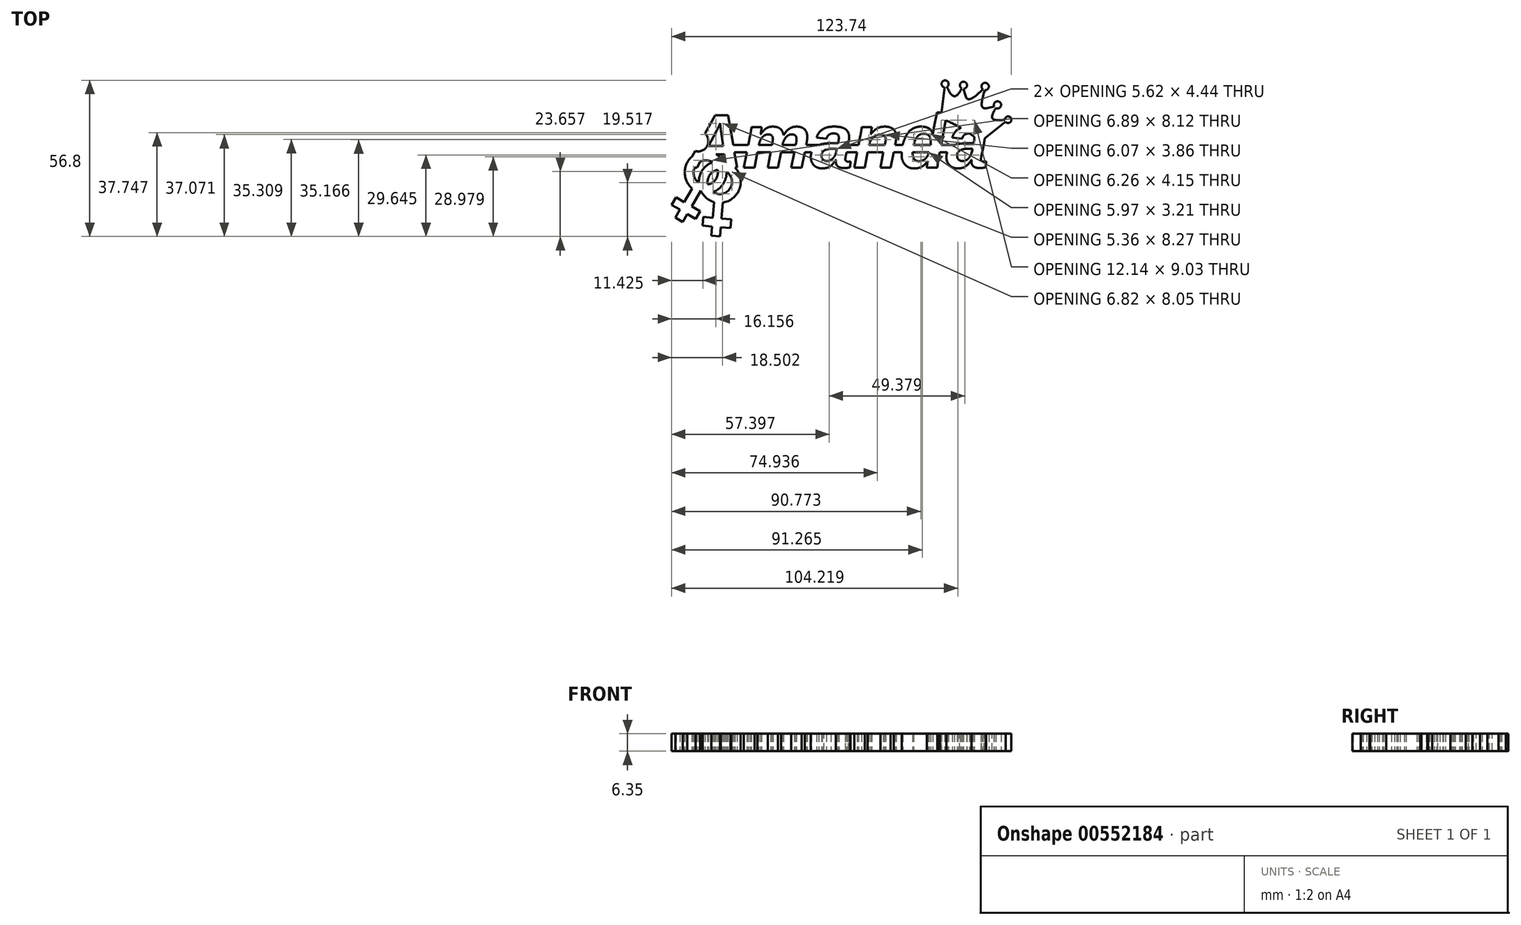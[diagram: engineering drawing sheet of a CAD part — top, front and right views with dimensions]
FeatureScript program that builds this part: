
annotation { "Feature Type Name" : "Feature", "Feature Type Description" : "" }
export const myFeature = defineFeature(function(context is Context, id is Id, definition is map)
    precondition{}
    {
        {
            var Q0;
            Q0=qCreatedBy(makeId("Top.planeOp"),FACE);
            var sketch = newSketch(context, id + "F0", { "sketchPlane" : qUnion([Q0])});
            skText(sketch, "E0", { "text": "Amanda", "fontName": "Arimo-BoldItalic.ttf"});
            skLineSegment(sketch, "E1.bottom", {"start": v(-56.87, 8.2) * mm, "end": v(37.6, 8.2) * mm});
            skLineSegment(sketch, "E1.top", {"start": v(-56.87, 5.54) * mm, "end": v(37.6, 5.54) * mm});
            skLineSegment(sketch, "E1.left", {"start": v(-56.87, 8.2) * mm, "end": v(-56.87, 5.54) * mm});
            skLineSegment(sketch, "E1.right", {"start": v(37.6, 8.2) * mm, "end": v(37.6, 5.54) * mm});
            skCircle(sketch, "E2", {"center": v(-65.8, 9.64) * mm, "radius": 3.75 * mm});
            const initialGuessF0  = {"E0": [-0.06965, 0, 1, 0, 0.02]};
            skSetInitialGuess(sketch, initialGuessF0);
            skSolve(sketch);
        }
        {
            var Q0;
            {var subQ0=sQuery(id+"F0.wireOp",EDGE,"E2");var subQ1=sQuery(id+"F0.wireOp",EDGE,"E0.sketch_text.stroke-4");var subQ2=makeQuery(id+"F0.imprint","INTERSECT",VERTEX,{"disambiguationData":[OD(0.0)],"derivedFrom":[subQ1,subQ0]});Q0=makeQuery(id+"F0.imprint","IMPRINT",FACE,{"disambiguationData":[TD([[makeQuery(id+"F0.imprint","IMPRINT",EDGE,{"disambiguationData":[TD([[subQ2,-1.0]])],"derivedFrom":subQ1}),1.0]])]});}
            var Q1;
            {var subQ0=sQuery(id+"F0.wireOp",EDGE,"E0.sketch_text.stroke-16");Q1=makeQuery(id+"F0.imprint","IMPRINT",FACE,{"disambiguationData":[TD([[makeQuery(id+"F0.imprint","IMPRINT",EDGE,{"derivedFrom":subQ0}),-1.0]])]});}
            var Q2;
            {var subQ0=sQuery(id+"F0.wireOp",EDGE,"E0.sketch_text.stroke-23");Q2=makeQuery(id+"F0.imprint","IMPRINT",FACE,{"disambiguationData":[TD([[makeQuery(id+"F0.imprint","IMPRINT",EDGE,{"derivedFrom":subQ0}),-1.0]])]});}
            var Q3;
            {var subQ0=sQuery(id+"F0.wireOp",EDGE,"E0.sketch_text.stroke-40");Q3=makeQuery(id+"F0.imprint","IMPRINT",FACE,{"disambiguationData":[TD([[makeQuery(id+"F0.imprint","IMPRINT",EDGE,{"derivedFrom":subQ0}),-1.0]])]});}
            var Q4;
            {var subQ0=sQuery(id+"F0.wireOp",EDGE,"E0.sketch_text.stroke-55");Q4=makeQuery(id+"F0.imprint","IMPRINT",FACE,{"disambiguationData":[TD([[makeQuery(id+"F0.imprint","IMPRINT",EDGE,{"derivedFrom":subQ0}),-1.0]])]});}
            var Q5;
            {var subQ0=sQuery(id+"F0.wireOp",EDGE,"E0.sketch_text.stroke-104");Q5=makeQuery(id+"F0.imprint","IMPRINT",FACE,{"disambiguationData":[TD([[makeQuery(id+"F0.imprint","IMPRINT",EDGE,{"derivedFrom":subQ0}),-1.0]])]});}
            var Q6;
            {var subQ0=sQuery(id+"F0.wireOp",EDGE,"E0.sketch_text.stroke-90");Q6=makeQuery(id+"F0.imprint","IMPRINT",FACE,{"disambiguationData":[TD([[makeQuery(id+"F0.imprint","IMPRINT",EDGE,{"derivedFrom":subQ0}),-1.0]])]});}
            var Q7;
            {var subQ0=sQuery(id+"F0.wireOp",EDGE,"E2");var subQ1=sQuery(id+"F0.wireOp",EDGE,"E0.sketch_text.stroke-4");var subQ2=makeQuery(id+"F0.imprint","INTERSECT",VERTEX,{"disambiguationData":[OD(0.0)],"derivedFrom":[subQ1,subQ0]});Q7=makeQuery(id+"F0.imprint","IMPRINT",FACE,{"disambiguationData":[TD([[makeQuery(id+"F0.imprint","IMPRINT",EDGE,{"disambiguationData":[TD([[subQ2,-1.0]])],"derivedFrom":subQ1}),-1.0]])]});}
            var Q8;
            {var subQ0=sQuery(id+"F0.wireOp",EDGE,"E1.bottom");var subQ1=sQuery(id+"F0.wireOp",EDGE,"E0.sketch_text.stroke-6");var subQ2=makeQuery(id+"F0.imprint","INTERSECT",VERTEX,{"derivedFrom":[subQ1,subQ0]});Q8=makeQuery(id+"F0.imprint","IMPRINT",FACE,{"disambiguationData":[TD([[makeQuery(id+"F0.imprint","IMPRINT",EDGE,{"disambiguationData":[TD([[subQ2,-1.0]])],"derivedFrom":subQ1}),1.0]])]});}
            var Q9;
            {var subQ3=sQuery(id+"F0.wireOp",EDGE,"E1.bottom");var subQ7=sQuery(id+"F0.wireOp",EDGE,"E0.sketch_text.stroke-39");var subQ8=makeQuery(id+"F0.imprint","INTERSECT",VERTEX,{"derivedFrom":[subQ7,subQ3]});Q9=makeQuery(id+"F0.imprint","IMPRINT",FACE,{"disambiguationData":[TD([[makeQuery(id+"F0.imprint","IMPRINT",EDGE,{"disambiguationData":[TD([[subQ8,-1.0]])],"derivedFrom":subQ7}),1.0]])]});}
            var Q10;
            Q10=makeQuery(id+"F0.imprint","IMPRINT",FACE,{"disambiguationData":[TD([[makeQuery(id+"F0.imprint","IMPRINT",EDGE,{"derivedFrom":sQuery(id+"F0.wireOp",EDGE,"E0.sketch_text.stroke-45")}),-1.0]])]});
            var Q11;
            {var subQ0=sQuery(id+"F0.wireOp",EDGE,"E1.bottom");var subQ1=sQuery(id+"F0.wireOp",EDGE,"E0.sketch_text.stroke-103");var subQ2=makeQuery(id+"F0.imprint","INTERSECT",VERTEX,{"derivedFrom":[subQ1,subQ0]});Q11=makeQuery(id+"F0.imprint","IMPRINT",FACE,{"disambiguationData":[TD([[makeQuery(id+"F0.imprint","IMPRINT",EDGE,{"disambiguationData":[TD([[subQ2,-1.0]])],"derivedFrom":subQ1}),1.0]])]});}
            var Q12;
            {var subQ0=sQuery(id+"F0.wireOp",EDGE,"E1.bottom");var subQ1=sQuery(id+"F0.wireOp",EDGE,"E0.sketch_text.stroke-118");var subQ2=makeQuery(id+"F0.imprint","INTERSECT",VERTEX,{"derivedFrom":[subQ1,subQ0]});Q12=makeQuery(id+"F0.imprint","IMPRINT",FACE,{"disambiguationData":[TD([[makeQuery(id+"F0.imprint","IMPRINT",EDGE,{"disambiguationData":[TD([[subQ2,-1.0]])],"derivedFrom":subQ1}),1.0]])]});}
            var Q13;
            Q13=makeQuery(id+"F0.imprint","IMPRINT",FACE,{"disambiguationData":[TD([[makeQuery(id+"F0.imprint","IMPRINT",EDGE,{"derivedFrom":sQuery(id+"F0.wireOp",EDGE,"E0.sketch_text.stroke-133")}),-1.0]])]});
            var Q14;
            Q14=makeQuery(id+"F0.imprint","IMPRINT",FACE,{"disambiguationData":[TD([[makeQuery(id+"F0.imprint","IMPRINT",EDGE,{"derivedFrom":sQuery(id+"F0.wireOp",EDGE,"E0.sketch_text.stroke-0")}),-1.0]])]});
            var Q15;
            {var subQ0=sQuery(id+"F0.wireOp",EDGE,"E1.bottom");var subQ1=sQuery(id+"F0.wireOp",EDGE,"E0.sketch_text.stroke-6");var subQ2=makeQuery(id+"F0.imprint","INTERSECT",VERTEX,{"derivedFrom":[subQ1,subQ0]});Q15=makeQuery(id+"F0.imprint","IMPRINT",FACE,{"disambiguationData":[TD([[makeQuery(id+"F0.imprint","IMPRINT",EDGE,{"disambiguationData":[TD([[subQ2,-1.0]])],"derivedFrom":subQ1}),-1.0]])]});}
            var Q16;
            {var subQ1=sQuery(id+"F0.wireOp",EDGE,"E0.sketch_text.stroke-85");var subQ7=sQuery(id+"F0.wireOp",EDGE,"E0.sketch_text.stroke-84");var subQ8=makeQuery(id+"F0.imprint","INTERSECT",VERTEX,{"derivedFrom":[subQ7,subQ1]});Q16=makeQuery(id+"F0.imprint","IMPRINT",FACE,{"disambiguationData":[TD([[makeQuery(id+"F0.imprint","IMPRINT",EDGE,{"disambiguationData":[TD([[subQ8,1.0]])],"derivedFrom":subQ7}),1.0]])]});}
            var Q17;
            {var subQ7=sQuery(id+"F0.wireOp",EDGE,"E0.sketch_text.stroke-86");Q17=makeQuery(id+"F0.imprint","IMPRINT",FACE,{"disambiguationData":[TD([[makeQuery(id+"F0.imprint","IMPRINT",EDGE,{"derivedFrom":subQ7}),-1.0]])]});}
            var Q18;
            Q18=makeQuery(id+"F0.imprint","IMPRINT",FACE,{"disambiguationData":[TD([[makeQuery(id+"F0.imprint","IMPRINT",EDGE,{"derivedFrom":sQuery(id+"F0.wireOp",EDGE,"E0.sketch_text.stroke-105")}),-1.0]])]});
            var Q19;
            {var subQ4=sQuery(id+"F0.wireOp",EDGE,"E0.sketch_text.stroke-110");Q19=makeQuery(id+"F0.imprint","IMPRINT",FACE,{"disambiguationData":[TD([[makeQuery(id+"F0.imprint","IMPRINT",EDGE,{"derivedFrom":subQ4}),-1.0]])]});}
            var Q20;
            Q20=makeQuery(id+"F0.imprint","IMPRINT",FACE,{"disambiguationData":[TD([[makeQuery(id+"F0.imprint","IMPRINT",EDGE,{"derivedFrom":sQuery(id+"F0.wireOp",EDGE,"E0.sketch_text.stroke-164")}),-1.0]])]});
            var Q21;
            {var subQ0=sQuery(id+"F0.wireOp",EDGE,"E1.top");var subQ1=sQuery(id+"F0.wireOp",EDGE,"E0.sketch_text.stroke-15");var subQ2=makeQuery(id+"F0.imprint","INTERSECT",VERTEX,{"derivedFrom":[subQ1,subQ0]});Q21=makeQuery(id+"F0.imprint","IMPRINT",FACE,{"disambiguationData":[TD([[makeQuery(id+"F0.imprint","IMPRINT",EDGE,{"disambiguationData":[TD([[subQ2,1.0]])],"derivedFrom":subQ1}),-1.0]])]});}
            var Q22;
            {var subQ0=sQuery(id+"F0.wireOp",EDGE,"E1.top");var subQ1=sQuery(id+"F0.wireOp",EDGE,"E0.sketch_text.stroke-22");var subQ2=makeQuery(id+"F0.imprint","INTERSECT",VERTEX,{"derivedFrom":[subQ1,subQ0]});Q22=makeQuery(id+"F0.imprint","IMPRINT",FACE,{"disambiguationData":[TD([[makeQuery(id+"F0.imprint","IMPRINT",EDGE,{"disambiguationData":[TD([[subQ2,1.0]])],"derivedFrom":subQ1}),-1.0]])]});}
            var Q23;
            {var subQ0=sQuery(id+"F0.wireOp",EDGE,"E1.bottom");var subQ1=sQuery(id+"F0.wireOp",EDGE,"E0.sketch_text.stroke-39");var subQ2=makeQuery(id+"F0.imprint","INTERSECT",VERTEX,{"derivedFrom":[subQ1,subQ0]});Q23=makeQuery(id+"F0.imprint","IMPRINT",FACE,{"disambiguationData":[TD([[makeQuery(id+"F0.imprint","IMPRINT",EDGE,{"disambiguationData":[TD([[subQ2,-1.0]])],"derivedFrom":subQ1}),-1.0]])]});}
            var Q24;
            {var subQ0=sQuery(id+"F0.wireOp",EDGE,"E0.sketch_text.stroke-85");var subQ1=sQuery(id+"F0.wireOp",EDGE,"E0.sketch_text.stroke-84");var subQ2=makeQuery(id+"F0.imprint","INTERSECT",VERTEX,{"derivedFrom":[subQ1,subQ0]});Q24=makeQuery(id+"F0.imprint","IMPRINT",FACE,{"disambiguationData":[TD([[makeQuery(id+"F0.imprint","IMPRINT",EDGE,{"disambiguationData":[TD([[subQ2,1.0]])],"derivedFrom":subQ1}),-1.0]])]});}
            var Q25;
            {var subQ0=sQuery(id+"F0.wireOp",EDGE,"E1.top");var subQ1=sQuery(id+"F0.wireOp",EDGE,"E0.sketch_text.stroke-89");var subQ2=makeQuery(id+"F0.imprint","INTERSECT",VERTEX,{"derivedFrom":[subQ1,subQ0]});Q25=makeQuery(id+"F0.imprint","IMPRINT",FACE,{"disambiguationData":[TD([[makeQuery(id+"F0.imprint","IMPRINT",EDGE,{"disambiguationData":[TD([[subQ2,1.0]])],"derivedFrom":subQ1}),-1.0]])]});}
            var Q26;
            {var subQ0=sQuery(id+"F0.wireOp",EDGE,"E1.top");var subQ1=sQuery(id+"F0.wireOp",EDGE,"E0.sketch_text.stroke-109");var subQ2=makeQuery(id+"F0.imprint","INTERSECT",VERTEX,{"derivedFrom":[subQ1,subQ0]});Q26=makeQuery(id+"F0.imprint","IMPRINT",FACE,{"disambiguationData":[TD([[makeQuery(id+"F0.imprint","IMPRINT",EDGE,{"disambiguationData":[TD([[subQ2,-1.0]])],"derivedFrom":subQ1}),-1.0]])]});}
            var Q27;
            {var subQ5=sQuery(id+"F0.wireOp",EDGE,"E1.bottom");var subQ6=sQuery(id+"F0.wireOp",EDGE,"E0.sketch_text.stroke-118");var subQ7=makeQuery(id+"F0.imprint","INTERSECT",VERTEX,{"derivedFrom":[subQ6,subQ5]});Q27=makeQuery(id+"F0.imprint","IMPRINT",FACE,{"disambiguationData":[TD([[makeQuery(id+"F0.imprint","IMPRINT",EDGE,{"disambiguationData":[TD([[subQ7,-1.0]])],"derivedFrom":subQ6}),-1.0]])]});}
            var Q28;
            Q28=makeQuery(id+"F0.imprint","IMPRINT",FACE,{"disambiguationData":[TD([[makeQuery(id+"F0.imprint","IMPRINT",EDGE,{"derivedFrom":sQuery(id+"F0.wireOp",EDGE,"E0.sketch_text.stroke-13")}),-1.0]])]});
            var Q29;
            Q29=makeQuery(id+"F0.imprint","IMPRINT",FACE,{"disambiguationData":[TD([[makeQuery(id+"F0.imprint","IMPRINT",EDGE,{"derivedFrom":sQuery(id+"F0.wireOp",EDGE,"E0.sketch_text.stroke-76")}),-1.0]])]});
            var Q30;
            {var subQ0=sQuery(id+"F0.wireOp",EDGE,"E1.bottom");var subQ1=sQuery(id+"F0.wireOp",EDGE,"E0.sketch_text.stroke-66");var subQ2=makeQuery(id+"F0.imprint","INTERSECT",VERTEX,{"derivedFrom":[subQ1,subQ0]});Q30=makeQuery(id+"F0.imprint","IMPRINT",FACE,{"disambiguationData":[TD([[makeQuery(id+"F0.imprint","IMPRINT",EDGE,{"disambiguationData":[TD([[subQ2,-1.0]])],"derivedFrom":subQ1}),1.0]])]});}
            var Q31;
            {var subQ0=sQuery(id+"F0.wireOp",EDGE,"E1.top");var subQ1=sQuery(id+"F0.wireOp",EDGE,"E0.sketch_text.stroke-17");var subQ2=makeQuery(id+"F0.imprint","INTERSECT",VERTEX,{"derivedFrom":[subQ1,subQ0]});Q31=makeQuery(id+"F0.imprint","IMPRINT",FACE,{"disambiguationData":[TD([[makeQuery(id+"F0.imprint","IMPRINT",EDGE,{"disambiguationData":[TD([[subQ2,-1.0]])],"derivedFrom":subQ1}),1.0]])]});}
            var Q32;
            {var subQ0=sQuery(id+"F0.wireOp",EDGE,"E1.top");var subQ1=sQuery(id+"F0.wireOp",EDGE,"E0.sketch_text.stroke-15");var subQ2=makeQuery(id+"F0.imprint","INTERSECT",VERTEX,{"derivedFrom":[subQ1,subQ0]});Q32=makeQuery(id+"F0.imprint","IMPRINT",FACE,{"disambiguationData":[TD([[makeQuery(id+"F0.imprint","IMPRINT",EDGE,{"disambiguationData":[TD([[subQ2,1.0]])],"derivedFrom":subQ1}),1.0]])]});}
            var Q33;
            {var subQ5=sQuery(id+"F0.wireOp",EDGE,"E0.sketch_text.stroke-126");var subQ6=sQuery(id+"F0.wireOp",EDGE,"E0.sketch_text.stroke-125");var subQ7=makeQuery(id+"F0.imprint","INTERSECT",VERTEX,{"derivedFrom":[subQ6,subQ5]});Q33=makeQuery(id+"F0.imprint","IMPRINT",FACE,{"disambiguationData":[TD([[makeQuery(id+"F0.imprint","IMPRINT",EDGE,{"disambiguationData":[TD([[subQ7,1.0]])],"derivedFrom":subQ6}),1.0]])]});}
            extrude(context, id + "F1", {"entities" : qUnion([Q0, Q1, Q2, Q3, Q4, Q5, Q6, Q7, Q8, Q9, Q10, Q11, Q12, Q13, Q14, Q15, Q16, Q17, Q18, Q19, Q20, Q21, Q22, Q23, Q24, Q25, Q26, Q27, Q28, Q29, Q30, Q31, Q32, Q33]), "depth" : 6.35 * mm, "offsetDistance" : 25.4 * mm});
        }
        {
            var Q0;
            Q0=qCreatedBy(makeId("Top.planeOp"),FACE);
            var sketch = newSketch(context, id + "F2", { "sketchPlane" : qUnion([Q0])});
            skCircle(sketch, "E3", {"center": v(24.15, 30.47) * mm, "radius": 1.29 * mm});
            skCircle(sketch, "E4", {"center": v(30.85, 29.98) * mm, "radius": 1.29 * mm});
            skCircle(sketch, "E5", {"center": v(38.74, 29.54) * mm, "radius": 1.34 * mm});
            skCircle(sketch, "E6", {"center": v(43.23, 22.83) * mm, "radius": 1.31 * mm});
            skCircle(sketch, "E7", {"center": v(47.1, 17.44) * mm, "radius": 1.2 * mm});
            skArc(sketch, "E8", {"start": v(36.96, 9.42) * mm, "mid": v(30.12, 14.34) * mm, "end": v(22.52, 17.98) * mm});
            skLineSegment(sketch, "E9", {"start": v(22.52, 17.98) * mm, "end": v(24.01, 29.19) * mm});
            skLineSegment(sketch, "E10", {"start": v(36.96, 9.42) * mm, "end": v(46.15, 16.72) * mm});
            skFitSpline(sketch, "E11", {"points": [v(24.83, 29.38) * mm, v(26.19, 26.87) * mm, v(27.5, 25.97) * mm, v(28.7, 26.52) * mm, v(30.2, 28.87) * mm], "startDerivative": vector(4.21, -9.4) * mm, "endDerivative": vector(4.9, 9.23) * mm});
            skFitSpline(sketch, "E12", {"points": [v(30.88, 28.7) * mm, v(31.53, 26.21) * mm, v(32.42, 24.96) * mm, v(34.21, 25.4) * mm, v(37.92, 28.47) * mm], "startDerivative": vector(2.23, -10.4) * mm, "endDerivative": vector(11.24, 10.52) * mm});
            skFitSpline(sketch, "E13", {"points": [v(38.61, 28.2) * mm, v(37.45, 23.38) * mm, v(37.98, 21.75) * mm, v(42.03, 22.3) * mm], "startDerivative": vector(-4, -13.13) * mm, "endDerivative": vector(13.55, 3.8) * mm});
            skFitSpline(sketch, "E14", {"points": [v(42.65, 21.66) * mm, v(41.4, 19.27) * mm, v(41.64, 17.66) * mm, v(45.9, 17.39) * mm], "startDerivative": vector(-4.66, -7.18) * mm, "endDerivative": vector(12.9, 1.1) * mm});
            skSolve(sketch);
        }
        {
            var Q0;
            Q0=makeQuery(id+"F2.imprint","IMPRINT",FACE,{"disambiguationData":[TD([[makeQuery(id+"F2.imprint","IMPRINT",EDGE,{"derivedFrom":sQuery(id+"F2.wireOp",EDGE,"E8")}),-1.0]])]});
            var Q1;
            {var subQ0=sQuery(id+"F2.wireOp",EDGE,"E5");var subQ1=makeQuery(id+"F2.imprint","INTERSECT",VERTEX,{"derivedFrom":[subQ0,sQuery(id+"F2.wireOp",EDGE,"E12")]});Q1=makeQuery(id+"F2.imprint","IMPRINT",FACE,{"disambiguationData":[TD([[makeQuery(id+"F2.imprint","IMPRINT",EDGE,{"disambiguationData":[TD([[subQ1,-1.0]])],"derivedFrom":subQ0}),1.0]])]});}
            var Q2;
            {var subQ0=sQuery(id+"F2.wireOp",EDGE,"E4");var subQ1=makeQuery(id+"F2.imprint","INTERSECT",VERTEX,{"derivedFrom":[subQ0,sQuery(id+"F2.wireOp",EDGE,"E11")]});Q2=makeQuery(id+"F2.imprint","IMPRINT",FACE,{"disambiguationData":[TD([[makeQuery(id+"F2.imprint","IMPRINT",EDGE,{"disambiguationData":[TD([[subQ1,-1.0]])],"derivedFrom":subQ0}),1.0]])]});}
            var Q3;
            {var subQ0=sQuery(id+"F2.wireOp",EDGE,"E3");var subQ1=makeQuery(id+"F2.imprint","INTERSECT",VERTEX,{"derivedFrom":[subQ0,sQuery(id+"F2.wireOp",EDGE,"E9")]});Q3=makeQuery(id+"F2.imprint","IMPRINT",FACE,{"disambiguationData":[TD([[makeQuery(id+"F2.imprint","IMPRINT",EDGE,{"disambiguationData":[TD([[subQ1,-1.0]])],"derivedFrom":subQ0}),1.0]])]});}
            var Q4;
            {var subQ0=sQuery(id+"F2.wireOp",EDGE,"E6");var subQ1=makeQuery(id+"F2.imprint","INTERSECT",VERTEX,{"derivedFrom":[subQ0,sQuery(id+"F2.wireOp",EDGE,"E13")]});Q4=makeQuery(id+"F2.imprint","IMPRINT",FACE,{"disambiguationData":[TD([[makeQuery(id+"F2.imprint","IMPRINT",EDGE,{"disambiguationData":[TD([[subQ1,-1.0]])],"derivedFrom":subQ0}),1.0]])]});}
            var Q5;
            {var subQ0=sQuery(id+"F2.wireOp",EDGE,"E7");var subQ1=makeQuery(id+"F2.imprint","INTERSECT",VERTEX,{"derivedFrom":[subQ0,sQuery(id+"F2.wireOp",EDGE,"E10")]});Q5=makeQuery(id+"F2.imprint","IMPRINT",FACE,{"disambiguationData":[TD([[makeQuery(id+"F2.imprint","IMPRINT",EDGE,{"disambiguationData":[TD([[subQ1,1.0]])],"derivedFrom":subQ0}),1.0]])]});}
            extrude(context, id + "F3", {"entities" : qUnion([Q0, Q1, Q2, Q3, Q4, Q5]), "operationType" : NewBodyOperationType.ADD, "depth" : 6.35 * mm, "offsetDistance" : 25.4 * mm});
        }
        {
            var Q0;
            Q0=qCreatedBy(makeId("Top.planeOp"),FACE);
            var sketch = newSketch(context, id + "F4", { "sketchPlane" : qUnion([Q0])});
            skCircle(sketch, "E15", {"center": v(-63.03, -1.76) * mm, "radius": 4.45 * mm});
            skCircle(sketch, "E16", {"center": v(-63.03, -1.76) * mm, "radius": 7.62 * mm});
            skLineSegment(sketch, "E17.bottom", {"start": v(-66.5, -5) * mm, "end": v(-63.75, -6.58) * mm});
            skLineSegment(sketch, "E17.top", {"start": v(-74.12, -18.19) * mm, "end": v(-71.37, -19.78) * mm});
            skLineSegment(sketch, "E17.left", {"start": v(-66.5, -5) * mm, "end": v(-74.12, -18.19) * mm});
            skLineSegment(sketch, "E17.right", {"start": v(-63.75, -6.58) * mm, "end": v(-71.37, -19.78) * mm});
            skLineSegment(sketch, "E18.bottom", {"start": v(-73.86, -10.79) * mm, "end": v(-65.06, -15.87) * mm});
            skLineSegment(sketch, "E18.top", {"start": v(-75.45, -13.53) * mm, "end": v(-66.65, -18.61) * mm});
            skLineSegment(sketch, "E18.left", {"start": v(-73.86, -10.79) * mm, "end": v(-75.45, -13.53) * mm});
            skLineSegment(sketch, "E18.right", {"start": v(-65.06, -15.87) * mm, "end": v(-66.65, -18.61) * mm});
            skLineSegment(sketch, "E19.1.0.0", {"start": v(-61, -24.76) * mm, "end": v(-57.84, -25.04) * mm});
            skLineSegment(sketch, "E19.1.0.1", {"start": v(-59.67, -9.58) * mm, "end": v(-61, -24.76) * mm});
            skLineSegment(sketch, "E19.1.0.2", {"start": v(-56.51, -9.86) * mm, "end": v(-57.84, -25.04) * mm});
            skLineSegment(sketch, "E19.1.0.3", {"start": v(-63.9, -17.94) * mm, "end": v(-53.78, -18.83) * mm});
            skCircle(sketch, "E19.1.0.4", {"center": v(-57.9, -5.19) * mm, "radius": 7.62 * mm});
            skLineSegment(sketch, "E19.1.0.5", {"start": v(-59.67, -9.58) * mm, "end": v(-56.51, -9.86) * mm});
            skCircle(sketch, "E19.1.0.6", {"center": v(-57.9, -5.19) * mm, "radius": 4.45 * mm});
            skLineSegment(sketch, "E19.1.0.7", {"start": v(-53.78, -18.83) * mm, "end": v(-54.05, -22) * mm});
            skLineSegment(sketch, "E19.1.0.8", {"start": v(-63.9, -17.94) * mm, "end": v(-64.18, -21.1) * mm});
            skLineSegment(sketch, "E19.1.0.9", {"start": v(-64.18, -21.1) * mm, "end": v(-54.05, -22) * mm});
            skSolve(sketch);
        }
        {
            var Q0;
            {var subQ5=sQuery(id+"F4.wireOp",EDGE,"E19.1.0.4");var subQ8=sQuery(id+"F4.wireOp",EDGE,"E15");var subQ9=makeQuery(id+"F4.imprint","INTERSECT",VERTEX,{"disambiguationData":[OD(0.0)],"derivedFrom":[subQ8,subQ5]});Q0=makeQuery(id+"F4.imprint","IMPRINT",FACE,{"disambiguationData":[TD([[makeQuery(id+"F4.imprint","IMPRINT",EDGE,{"disambiguationData":[TD([[subQ9,-1.0]])],"derivedFrom":subQ8}),-1.0]])]});}
            var Q1;
            {var subQ1=sQuery(id+"F4.wireOp",EDGE,"E16");var subQ5=sQuery(id+"F4.wireOp",EDGE,"E17.left");var subQ8=makeQuery(id+"F4.imprint","INTERSECT",VERTEX,{"derivedFrom":[subQ1,subQ5]});Q1=makeQuery(id+"F4.imprint","IMPRINT",FACE,{"disambiguationData":[TD([[makeQuery(id+"F4.imprint","IMPRINT",EDGE,{"disambiguationData":[TD([[subQ8,-1.0]])],"derivedFrom":subQ1}),1.0]])]});}
            var Q2;
            {var subQ0=sQuery(id+"F4.wireOp",EDGE,"E17.right");var subQ1=sQuery(id+"F4.wireOp",EDGE,"E17.bottom");var subQ2=makeQuery(id+"F4.imprint","INTERSECT",VERTEX,{"derivedFrom":[subQ1,subQ0]});Q2=makeQuery(id+"F4.imprint","IMPRINT",FACE,{"disambiguationData":[TD([[makeQuery(id+"F4.imprint","IMPRINT",EDGE,{"disambiguationData":[TD([[subQ2,1.0]])],"derivedFrom":subQ1}),-1.0]])]});}
            var Q3;
            {var subQ3=sQuery(id+"F4.wireOp",EDGE,"E19.1.0.4");var subQ5=sQuery(id+"F4.wireOp",EDGE,"E15");var subQ6=makeQuery(id+"F4.imprint","INTERSECT",VERTEX,{"disambiguationData":[OD(1.0)],"derivedFrom":[subQ5,subQ3]});Q3=makeQuery(id+"F4.imprint","IMPRINT",FACE,{"disambiguationData":[TD([[makeQuery(id+"F4.imprint","IMPRINT",EDGE,{"disambiguationData":[TD([[subQ6,-1.0]])],"derivedFrom":subQ5}),-1.0]])]});}
            var Q4;
            {var subQ0=sQuery(id+"F4.wireOp",EDGE,"E19.1.0.6");var subQ1=sQuery(id+"F4.wireOp",EDGE,"E15");var subQ2=makeQuery(id+"F4.imprint","INTERSECT",VERTEX,{"disambiguationData":[OD(0.0)],"derivedFrom":[subQ1,subQ0]});Q4=makeQuery(id+"F4.imprint","IMPRINT",FACE,{"disambiguationData":[TD([[makeQuery(id+"F4.imprint","IMPRINT",EDGE,{"disambiguationData":[TD([[subQ2,1.0]])],"derivedFrom":subQ1}),-1.0]])]});}
            var Q5;
            {var subQ0=sQuery(id+"F4.wireOp",EDGE,"E19.1.0.4");var subQ1=sQuery(id+"F4.wireOp",EDGE,"E15");var subQ2=makeQuery(id+"F4.imprint","INTERSECT",VERTEX,{"disambiguationData":[OD(0.0)],"derivedFrom":[subQ1,subQ0]});Q5=makeQuery(id+"F4.imprint","IMPRINT",FACE,{"disambiguationData":[TD([[makeQuery(id+"F4.imprint","IMPRINT",EDGE,{"disambiguationData":[TD([[subQ2,1.0]])],"derivedFrom":subQ1}),1.0]])]});}
            var Q6;
            {var subQ0=sQuery(id+"F4.wireOp",EDGE,"E19.1.0.4");var subQ1=sQuery(id+"F4.wireOp",EDGE,"E15");var subQ2=makeQuery(id+"F4.imprint","INTERSECT",VERTEX,{"disambiguationData":[OD(0.0)],"derivedFrom":[subQ1,subQ0]});Q6=makeQuery(id+"F4.imprint","IMPRINT",FACE,{"disambiguationData":[TD([[makeQuery(id+"F4.imprint","IMPRINT",EDGE,{"disambiguationData":[TD([[subQ2,1.0]])],"derivedFrom":subQ1}),-1.0]])]});}
            var Q7;
            {var subQ0=sQuery(id+"F4.wireOp",EDGE,"E19.1.0.5");Q7=makeQuery(id+"F4.imprint","IMPRINT",FACE,{"disambiguationData":[TD([[makeQuery(id+"F4.imprint","IMPRINT",EDGE,{"derivedFrom":subQ0}),-1.0]])]});}
            var Q8;
            {var subQ0=sQuery(id+"F4.wireOp",EDGE,"E19.1.0.4");var subQ1=sQuery(id+"F4.wireOp",EDGE,"E19.1.0.1");var subQ2=makeQuery(id+"F4.imprint","INTERSECT",VERTEX,{"derivedFrom":[subQ1,subQ0]});Q8=makeQuery(id+"F4.imprint","IMPRINT",FACE,{"disambiguationData":[TD([[makeQuery(id+"F4.imprint","IMPRINT",EDGE,{"disambiguationData":[TD([[subQ2,-1.0]])],"derivedFrom":subQ1}),1.0]])]});}
            var Q9;
            {var subQ0=sQuery(id+"F4.wireOp",EDGE,"E19.1.0.3");var subQ1=sQuery(id+"F4.wireOp",EDGE,"E19.1.0.1");var subQ2=makeQuery(id+"F4.imprint","INTERSECT",VERTEX,{"derivedFrom":[subQ1,subQ0]});Q9=makeQuery(id+"F4.imprint","IMPRINT",FACE,{"disambiguationData":[TD([[makeQuery(id+"F4.imprint","IMPRINT",EDGE,{"disambiguationData":[TD([[subQ2,-1.0]])],"derivedFrom":subQ1}),1.0]])]});}
            var Q10;
            {var subQ0=sQuery(id+"F4.wireOp",EDGE,"E19.1.0.0");Q10=makeQuery(id+"F4.imprint","IMPRINT",FACE,{"disambiguationData":[TD([[makeQuery(id+"F4.imprint","IMPRINT",EDGE,{"derivedFrom":subQ0}),1.0]])]});}
            var Q11;
            {var subQ5=sQuery(id+"F4.wireOp",EDGE,"E19.1.0.7");Q11=makeQuery(id+"F4.imprint","IMPRINT",FACE,{"disambiguationData":[TD([[makeQuery(id+"F4.imprint","IMPRINT",EDGE,{"derivedFrom":subQ5}),-1.0]])]});}
            var Q12;
            {var subQ5=sQuery(id+"F4.wireOp",EDGE,"E19.1.0.8");Q12=makeQuery(id+"F4.imprint","IMPRINT",FACE,{"disambiguationData":[TD([[makeQuery(id+"F4.imprint","IMPRINT",EDGE,{"derivedFrom":subQ5}),1.0]])]});}
            var Q13;
            {var subQ5=sQuery(id+"F4.wireOp",EDGE,"E18.right");Q13=makeQuery(id+"F4.imprint","IMPRINT",FACE,{"disambiguationData":[TD([[makeQuery(id+"F4.imprint","IMPRINT",EDGE,{"derivedFrom":subQ5}),-1.0]])]});}
            var Q14;
            {var subQ0=sQuery(id+"F4.wireOp",EDGE,"E17.top");Q14=makeQuery(id+"F4.imprint","IMPRINT",FACE,{"disambiguationData":[TD([[makeQuery(id+"F4.imprint","IMPRINT",EDGE,{"derivedFrom":subQ0}),1.0]])]});}
            var Q15;
            {var subQ0=sQuery(id+"F4.wireOp",EDGE,"E17.left");var subQ1=sQuery(id+"F4.wireOp",EDGE,"E16");var subQ2=makeQuery(id+"F4.imprint","INTERSECT",VERTEX,{"derivedFrom":[subQ1,subQ0]});Q15=makeQuery(id+"F4.imprint","IMPRINT",FACE,{"disambiguationData":[TD([[makeQuery(id+"F4.imprint","IMPRINT",EDGE,{"disambiguationData":[TD([[subQ2,-1.0]])],"derivedFrom":subQ1}),-1.0]])]});}
            var Q16;
            {var subQ5=sQuery(id+"F4.wireOp",EDGE,"E18.left");Q16=makeQuery(id+"F4.imprint","IMPRINT",FACE,{"disambiguationData":[TD([[makeQuery(id+"F4.imprint","IMPRINT",EDGE,{"derivedFrom":subQ5}),1.0]])]});}
            var Q17;
            {var subQ0=sQuery(id+"F4.wireOp",EDGE,"E18.bottom");var subQ1=sQuery(id+"F4.wireOp",EDGE,"E17.left");var subQ2=makeQuery(id+"F4.imprint","INTERSECT",VERTEX,{"derivedFrom":[subQ1,subQ0]});Q17=makeQuery(id+"F4.imprint","IMPRINT",FACE,{"disambiguationData":[TD([[makeQuery(id+"F4.imprint","IMPRINT",EDGE,{"disambiguationData":[TD([[subQ2,-1.0]])],"derivedFrom":subQ1}),1.0]])]});}
            var Q18;
            {var subQ0=sQuery(id+"F4.wireOp",EDGE,"E19.1.0.5");Q18=makeQuery(id+"F4.imprint","IMPRINT",FACE,{"disambiguationData":[TD([[makeQuery(id+"F4.imprint","IMPRINT",EDGE,{"derivedFrom":subQ0}),1.0]])]});}
            extrude(context, id + "F5", {"entities" : qUnion([Q0, Q1, Q2, Q3, Q4, Q5, Q6, Q7, Q8, Q9, Q10, Q11, Q12, Q13, Q14, Q15, Q16, Q17, Q18]), "operationType" : NewBodyOperationType.ADD, "depth" : 6.35 * mm, "offsetDistance" : 25.4 * mm});
        }
    });
